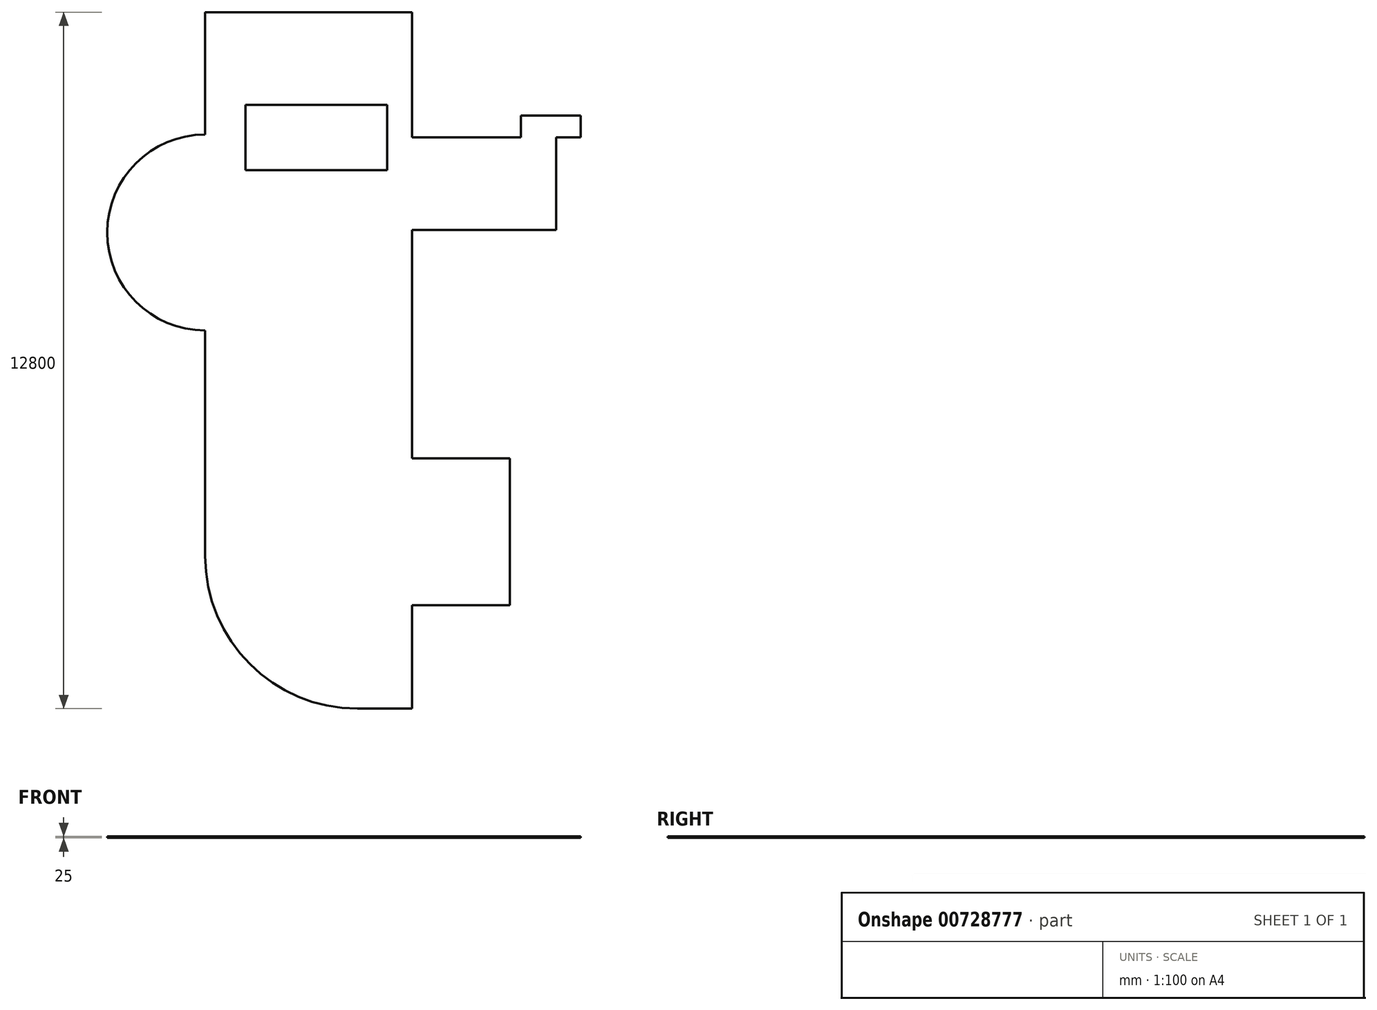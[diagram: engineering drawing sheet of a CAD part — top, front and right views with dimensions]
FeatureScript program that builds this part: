
annotation { "Feature Type Name" : "Feature", "Feature Type Description" : "" }
export const myFeature = defineFeature(function(context is Context, id is Id, definition is map)
    precondition{}
    {
        {
            var Q0;
            Q0=qCreatedBy(makeId("Top.planeOp"),FACE);
            var sketch = newSketch(context, id + "F0", { "sketchPlane" : qUnion([Q0])});
            skLineSegment(sketch, "E0.bottom", {"start": v(1900, -6400) * mm, "end": v(-1900, -6400) * mm});
            skLineSegment(sketch, "E0.top", {"start": v(1900, 6400) * mm, "end": v(-1900, 6400) * mm});
            skLineSegment(sketch, "E0.left", {"start": v(1900, -6400) * mm, "end": v(1900, 6400) * mm});
            skLineSegment(sketch, "E0.right", {"start": v(-1900, -6400) * mm, "end": v(-1900, 6400) * mm});
            skPoint(sketch, "E0.middle", {"position": v(0, 0) * mm});
            skLineSegment(sketch, "E1", {"start": v(-1900, 6400) * mm, "end": v(-1900, 4150) * mm, "construction": true});
            skLineSegment(sketch, "E2", {"start": v(-1900, 4150) * mm, "end": v(-1900, 2350) * mm, "construction": true});
            skArc(sketch, "E3", {"start": v(-1900, 4150) * mm, "mid": v(-3700, 2350) * mm, "end": v(-1900, 550) * mm});
            skLineSegment(sketch, "E4", {"start": v(1900, 6400) * mm, "end": v(1900, 4100) * mm, "construction": true});
            skLineSegment(sketch, "E5", {"start": v(1900, 4100) * mm, "end": v(5000, 4100) * mm});
            skLineSegment(sketch, "E6", {"start": v(1900, 4100) * mm, "end": v(3900, 4100) * mm, "construction": true});
            skLineSegment(sketch, "E7", {"start": v(3900, 4100) * mm, "end": v(3900, 4500) * mm});
            skLineSegment(sketch, "E8", {"start": v(3900, 4500) * mm, "end": v(5000, 4500) * mm});
            skLineSegment(sketch, "E9", {"start": v(5000, 4500) * mm, "end": v(5000, 4100) * mm});
            skLineSegment(sketch, "E10", {"start": v(5000, 4100) * mm, "end": v(4550, 4100) * mm, "construction": true});
            skLineSegment(sketch, "E11", {"start": v(5000, 4500) * mm, "end": v(5000, 2400) * mm, "construction": true});
            skLineSegment(sketch, "E12", {"start": v(5000, 2400) * mm, "end": v(1900, 2400) * mm, "construction": true});
            skLineSegment(sketch, "E13", {"start": v(4550, 4100) * mm, "end": v(4550, 2400) * mm});
            skLineSegment(sketch, "E14", {"start": v(4550, 2400) * mm, "end": v(1900, 2400) * mm});
            skLineSegment(sketch, "E15", {"start": v(1900, 2400) * mm, "end": v(1900, -1800) * mm, "construction": true});
            skLineSegment(sketch, "E16", {"start": v(1900, -1800) * mm, "end": v(3700, -1800) * mm});
            skLineSegment(sketch, "E17", {"start": v(3700, -1800) * mm, "end": v(3700, -4500) * mm});
            skLineSegment(sketch, "E18", {"start": v(3700, -4500) * mm, "end": v(1900, -4500) * mm});
            skLineSegment(sketch, "E19", {"start": v(-1900, -6400) * mm, "end": v(900, -6400) * mm, "construction": true});
            skLineSegment(sketch, "E20", {"start": v(-1900, -6400) * mm, "end": v(-1900, -3600) * mm, "construction": true});
            skArc(sketch, "E21", {"start": v(-1900, -3600) * mm, "mid": v(-1079.9, -5579.9) * mm, "end": v(900, -6400) * mm});
            skLineSegment(sketch, "E22.bottom", {"start": v(-1158.02, 4693.54) * mm, "end": v(1441.98, 4693.54) * mm});
            skLineSegment(sketch, "E22.top", {"start": v(-1158.02, 3493.54) * mm, "end": v(1441.98, 3493.54) * mm});
            skLineSegment(sketch, "E22.left", {"start": v(-1158.02, 4693.54) * mm, "end": v(-1158.02, 3493.54) * mm});
            skLineSegment(sketch, "E22.right", {"start": v(1441.98, 4693.54) * mm, "end": v(1441.98, 3493.54) * mm});
            skSolve(sketch);
        }
        {
            var Q0;
            {var subQ0=sQuery(id+"F0.wireOp",EDGE,"E16");Q0=makeQuery(id+"F0.imprint","IMPRINT",FACE,{"disambiguationData":[TD([[makeQuery(id+"F0.imprint","IMPRINT",EDGE,{"derivedFrom":subQ0}),-1.0]])]});}
            var Q1;
            {var subQ0=sQuery(id+"F0.wireOp",EDGE,"E3");Q1=makeQuery(id+"F0.imprint","IMPRINT",FACE,{"disambiguationData":[TD([[makeQuery(id+"F0.imprint","IMPRINT",EDGE,{"derivedFrom":subQ0}),1.0]])]});}
            var Q2;
            {var subQ0=sQuery(id+"F0.wireOp",EDGE,"E7");Q2=makeQuery(id+"F0.imprint","IMPRINT",FACE,{"disambiguationData":[TD([[makeQuery(id+"F0.imprint","IMPRINT",EDGE,{"derivedFrom":subQ0}),-1.0]])]});}
            var Q3;
            {var subQ0=sQuery(id+"F0.wireOp",EDGE,"E13");Q3=makeQuery(id+"F0.imprint","IMPRINT",FACE,{"disambiguationData":[TD([[makeQuery(id+"F0.imprint","IMPRINT",EDGE,{"derivedFrom":subQ0}),-1.0]])]});}
            var Q4;
            {var subQ6=sQuery(id+"F0.wireOp",EDGE,"E0.top");Q4=makeQuery(id+"F0.imprint","IMPRINT",FACE,{"disambiguationData":[TD([[makeQuery(id+"F0.imprint","IMPRINT",EDGE,{"derivedFrom":subQ6}),1.0]])]});}
            extrude(context, id + "F1", {"entities" : qUnion([Q0, Q1, Q2, Q3, Q4]), "depth" : 25 * mm, "offsetDistance" : 25 * mm});
        }
    });
